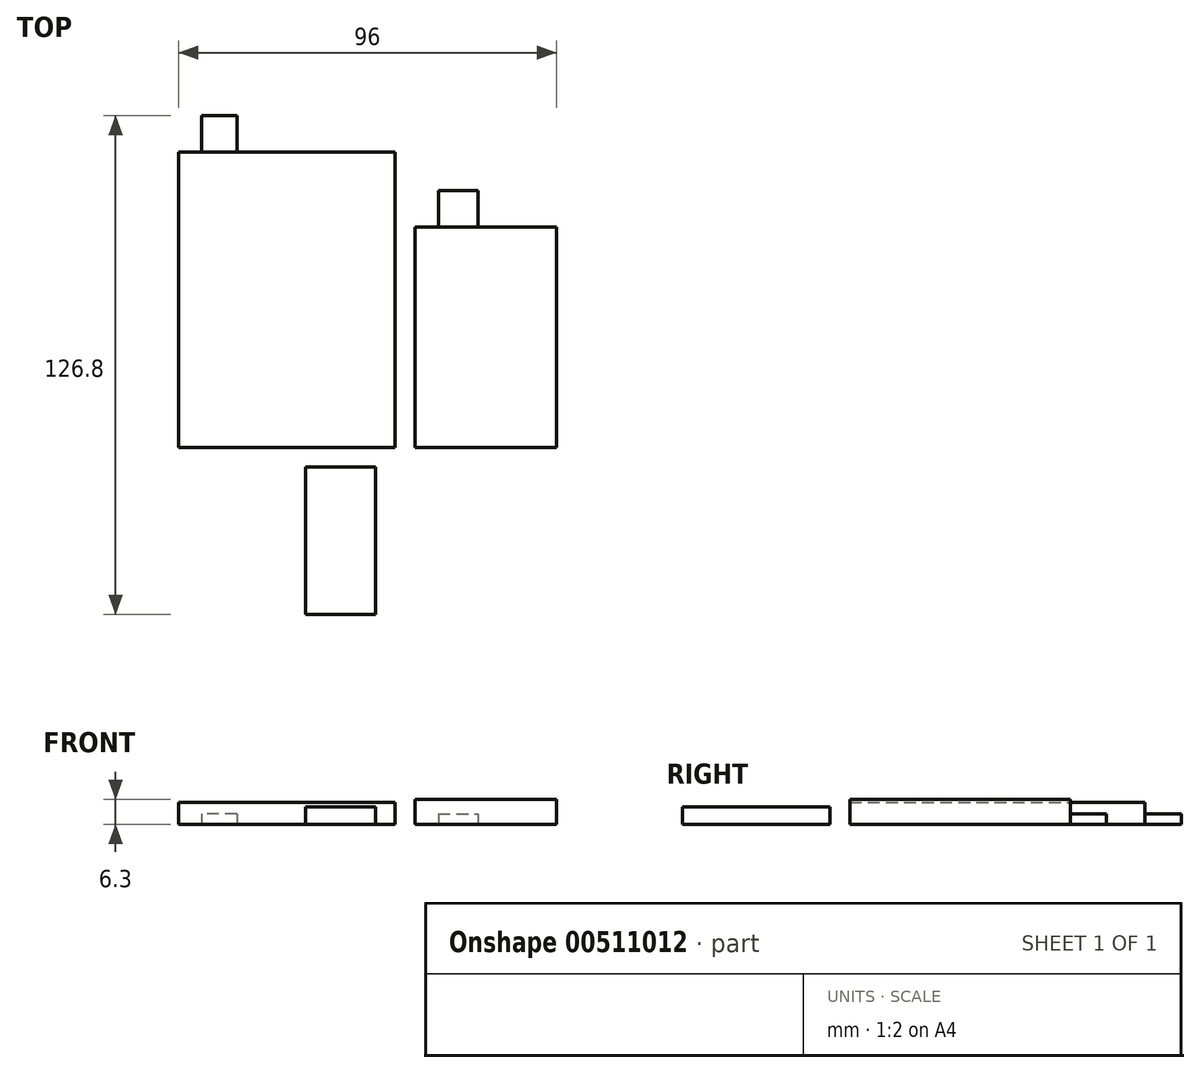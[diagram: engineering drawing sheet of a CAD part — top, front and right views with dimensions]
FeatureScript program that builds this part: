
annotation { "Feature Type Name" : "Feature", "Feature Type Description" : "" }
export const myFeature = defineFeature(function(context is Context, id is Id, definition is map)
    precondition{}
    {
        {
            var Q0;
            Q0=qCreatedBy(makeId("Top.planeOp"),FACE);
            var sketch = newSketch(context, id + "F0", { "sketchPlane" : qUnion([Q0])});
            skLineSegment(sketch, "E0.bottom", {"start": v(0, 0) * mm, "end": v(-55, 0) * mm});
            skLineSegment(sketch, "E0.top", {"start": v(0, 75) * mm, "end": v(-55, 75) * mm});
            skLineSegment(sketch, "E0.left", {"start": v(0, 0) * mm, "end": v(0, 75) * mm});
            skLineSegment(sketch, "E0.right", {"start": v(-55, 0) * mm, "end": v(-55, 75) * mm});
            skLineSegment(sketch, "E1", {"start": v(-49.2, 75) * mm, "end": v(-49.2, 84.3) * mm});
            skLineSegment(sketch, "E2", {"start": v(-49.2, 84.3) * mm, "end": v(-40.2, 84.3) * mm});
            skLineSegment(sketch, "E3", {"start": v(-40.2, 84.3) * mm, "end": v(-40.2, 75) * mm});
            skSolve(sketch);
        }
        {
            var Q0;
            Q0=makeQuery(id+"F0.imprint","IMPRINT",FACE,{"disambiguationData":[TD([[makeQuery(id+"F0.imprint","IMPRINT",EDGE,{"derivedFrom":sQuery(id+"F0.wireOp",EDGE,"E0.bottom")}),-1.0]])]});
            extrude(context, id + "F1", {"entities" : qUnion([Q0]), "depth" : 5.6 * mm, "offsetDistance" : 25 * mm});
        }
        {
            var Q0;
            {var subQ0=sQuery(id+"F0.wireOp",EDGE,"E1");Q0=makeQuery(id+"F0.imprint","IMPRINT",FACE,{"disambiguationData":[TD([[makeQuery(id+"F0.imprint","IMPRINT",EDGE,{"derivedFrom":subQ0}),-1.0]])]});}
            extrude(context, id + "F2", {"entities" : qUnion([Q0]), "operationType" : NewBodyOperationType.ADD, "depth" : 2.6 * mm, "offsetDistance" : 25 * mm});
        }
        {
            var Q0;
            Q0=qCreatedBy(makeId("Top.planeOp"),FACE);
            var sketch = newSketch(context, id + "F3", { "sketchPlane" : qUnion([Q0])});
            skLineSegment(sketch, "E4.bottom", {"start": v(5, 0) * mm, "end": v(41, 0) * mm});
            skLineSegment(sketch, "E4.top", {"start": v(5, 56) * mm, "end": v(41, 56) * mm});
            skLineSegment(sketch, "E4.left", {"start": v(5, 0) * mm, "end": v(5, 56) * mm});
            skLineSegment(sketch, "E4.right", {"start": v(41, 0) * mm, "end": v(41, 56) * mm});
            skLineSegment(sketch, "E5", {"start": v(11, 56) * mm, "end": v(11, 65.2) * mm});
            skLineSegment(sketch, "E6", {"start": v(11, 65.2) * mm, "end": v(21, 65.2) * mm});
            skLineSegment(sketch, "E7", {"start": v(21, 65.2) * mm, "end": v(21, 56) * mm});
            skSolve(sketch);
        }
        {
            var Q0;
            Q0=makeQuery(id+"F3.imprint","IMPRINT",FACE,{"disambiguationData":[TD([[makeQuery(id+"F3.imprint","IMPRINT",EDGE,{"derivedFrom":sQuery(id+"F3.wireOp",EDGE,"E4.bottom")}),1.0]])]});
            extrude(context, id + "F4", {"entities" : qUnion([Q0]), "depth" : 6.3 * mm, "offsetDistance" : 25 * mm});
        }
        {
            var Q0;
            {var subQ0=sQuery(id+"F3.wireOp",EDGE,"E5");Q0=makeQuery(id+"F3.imprint","IMPRINT",FACE,{"disambiguationData":[TD([[makeQuery(id+"F3.imprint","IMPRINT",EDGE,{"derivedFrom":subQ0}),-1.0]])]});}
            extrude(context, id + "F5", {"entities" : qUnion([Q0]), "operationType" : NewBodyOperationType.ADD, "depth" : 2.6 * mm, "offsetDistance" : 25 * mm});
        }
        {
            var Q0;
            Q0=qCreatedBy(makeId("Top.planeOp"),FACE);
            var sketch = newSketch(context, id + "F6", { "sketchPlane" : qUnion([Q0])});
            skLineSegment(sketch, "E8.bottom", {"start": v(-5, -5) * mm, "end": v(-22.75, -5) * mm});
            skLineSegment(sketch, "E8.top", {"start": v(-5, -42.5) * mm, "end": v(-22.75, -42.5) * mm});
            skLineSegment(sketch, "E8.left", {"start": v(-5, -5) * mm, "end": v(-5, -42.5) * mm});
            skLineSegment(sketch, "E8.right", {"start": v(-22.75, -5) * mm, "end": v(-22.75, -42.5) * mm});
            skSolve(sketch);
        }
        {
            var Q0;
            Q0=makeQuery(id+"F6.imprint","IMPRINT",FACE,{"disambiguationData":[TD([[makeQuery(id+"F6.imprint","IMPRINT",EDGE,{"derivedFrom":sQuery(id+"F6.wireOp",EDGE,"E8.bottom")}),1.0]])]});
            extrude(context, id + "F7", {"entities" : qUnion([Q0]), "depth" : 4.5 * mm, "offsetDistance" : 25 * mm});
        }
    });
